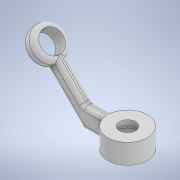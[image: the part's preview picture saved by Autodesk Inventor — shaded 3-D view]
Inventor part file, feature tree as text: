
AUTODESK INVENTOR PART (.ipt)
format: ipt  version: 2022 (Build 260153000, 153)  size: 220,672 bytes
history: native  units: mm
features: extrude x8, sketch x8, fillet x2, other x1
ambient origin geometry x8: Origin, YZ Plane, XZ Plane, XY Plane, X Axis, Y Axis, Z Axis, Center Point
bodies: Body1 (feature_tree)
feature tree (19):
  other  "Bryła1"
  extrude  "Wyciągnięcie proste1"  Depth=40.0mm
  extrude  "Wyciągnięcie proste3"  Depth=20.0mm TaperAngle=0.0deg
  extrude  "Wyciągnięcie proste4"  TaperAngle=45.0deg  [1 undecoded]
  extrude  "Wyciągnięcie proste5"  Depth=112.0mm
  fillet  "Zaokrąglenie1"  Radius=20.0mm
  extrude  "Wyciągnięcie proste7"  Depth=40.0mm
  extrude  "Wyciągnięcie proste8"  Depth=10.0mm TaperAngle=0.0deg
  extrude  "Wyciągnięcie proste9"  Depth=22.0mm
  extrude  "Wyciągnięcie proste10"  Depth=5.0mm
  fillet  "Zaokrąglenie2"  Radius=10.0mm
  sketch  "Szkic1"
  sketch  "Szkic3"
  sketch  "Szkic4"
  sketch  "Szkic5"
  sketch  "Szkic7"
  sketch  "Szkic8"
  sketch  "Szkic9"
  sketch  "Szkic10"
note: 1 required parameter value undecoded (feature->parameter linkage not recoverable at this tier; creation-order binding heuristic only, values carry confidence <= 0.55)
